# Revit family: 482069001(1)
name_source: partatom
category: Generic Models
units: mm (PartAtom-declared; Revit-internal decimal feet)

## family parameters
Always vertical = Yes
Can host rebar = No
Cut with Voids When Loaded = No
Host = Floor
Room Calculation Point = No
Shared = Yes

## types (1)
- 482069001
    ARTICLENO = NB
    BEZ = Balkonpot Pluvetta® 50-60 mm met 90° bocht van PVC met 70 mm spi-eind, zonder rooster
    BOMINFO = LINA
    CATALOG = König & Ronneberger
    CNSORDERNO = 482069001
    D = 108 mm  [stored 0.354331 ft]
    D1 = 94 mm  [stored 0.308399 ft]
    D2 = 70 mm  [stored 0.229659 ft]
    Description = Balcony transit and drain wastes
    H = 121 mm  [stored 0.396982 ft]
    H1 = 86 mm  [stored 0.282152 ft]
    HTML = Product page
    INFO = PDF Catalog
    LINA = 482069001
    LODLEVEL = 300
    Manufacturer = KOERO
    Model = 482069001
    NB = 482069001(1)
    NBSYN = $CNSORDERNO.($LODLEVEL.)
    NN = PLUVETTA® 90°
    NT = Balcony transit and drain wastes
    SUPPLIER = KOERO

note: [stored X ft] marks values corroborated as IEEE doubles in the binary element streams (Revit-internal decimal feet)

## geometry (parser evidence)
native form markers: Sweep x6
no freeform markers — native parametric forms only
